# Revit family: QF_BOURGEAT_Satellite4G_froid_1-1_entree325_pleine
name_source: partatom
category: Equipement spécialisé
revit_build: Autodesk Revit 2015 (Build: 20140606_1530(x64)
units: mm (PartAtom-declared; Revit-internal decimal feet)

## types (2) — shared parameters
Certification = NF hygiene alimentaire
Charge max = 140.00 kg
Charge_gaz = 0.150 Kg
Classe Climatique = 4
Consommation énergétique = 3.2Kwh/h NFD40-016
Diametre_roue = 160 mm  [stored 0.524934 ft]
Fabricant = BOURGEAT
Fréquence = 50 Hz
Hauteur hors tout = 1575 mm  [stored 5.16732 ft]
Hauteur_poignee_porte_sol = 600 mm
Hauteur_poignees_laterales = 937 mm  [stored 3.07415 ft]
Hauteur_porte = 1328 mm  [stored 4.35696 ft]
Hauteur_roue = 200 mm  [stored 0.656168 ft]
Indice de protection = IP25
Intensité nominale = 1 A
Largeur_porte = 500 mm  [stored 1.64042 ft]
Longueur hors tout = 585 mm  [stored 1.91929 ft]
Longueur_poignees_laterales = 755 mm  [stored 2.47703 ft]
Materiau_Poignee_porte = B_Elastomère_TPE_S
Materiau_bac = B_Elastomère_TPE_S
Materiau_bandage = B_Elastomère_TPE_S
Materiau_porte = Acier inoxydable, brossé
Materiau_vitre = Verre, vitrage transparent, trempé
Nature isolant = Mousse sans PU
Phase = 2
Poids net à vide = 90.00 kg
Pos_V_IHM = 38 mm  [stored 0.124672 ft]
Profondeur hors tout = 911 mm  [stored 2.98885 ft]
Puissance frigorifique = 270 W à -5°C
Puissance électrique  = 300 W
Spécification du Fabricant = Satellite 4G
Tension = 230 V
Type Fluide Frigorigène = R134a
URL catalogue = http://www.bourgeat.fr

## per-type parameters (varying)
| type | Modèle | Poignee_droite | Poignee_gauche |
| GN14_porte_inox_tirant_droit | 842014 + 844000 | Oui | Non |
| GN14_porte_inox_tirant_gauche | 842014 | Non | Oui |

note: [stored X ft] marks values corroborated as IEEE doubles in the binary element streams (Revit-internal decimal feet)
